# Revit family: MUEBLE SUNSET 600 TEAK
name_source: partatom
category: Generic Models
units: mm (PartAtom-declared; Revit-internal decimal feet)

## family parameters
Always vertical = Yes
Can host rebar = No
Cut with Voids When Loaded = No
Part Type = Normal
Room Calculation Point = No
Round Connector Dimension = Use Diameter
Shared = No
Work Plane-Based = No

## types (12) — shared parameters
Ancho tirador = 250 mm  [stored 0.82021 ft]
Material cubierta = Loza blanco brillo
Material tirador = Acero semi pulido
Profundidad receptáculo = 150 mm

## per-type parameters (varying)
| type | Ancho | Ancho borde cub | Largo | Largo receptáculo | Material costados | Material frentes | Prof borde cub trasero | Prof lavamanos |
| ORANS Mueble Orlando Fume (MFC 034) 060,5cm ancho | 480 mm  [stored 1.5748 ft] | 40 mm | 600 mm | 460 mm  [stored 1.50919 ft] | Fume (MFC 034) vertical | Fume (MFC 034) horizontal | 120 mm  [stored 0.393701 ft] | 320 mm  [stored 1.04987 ft] |
| ORANS Mueble Orlando Fume (MFC 034) 070,5cm ancho | 465 mm | 70 mm | 705 mm | 460 mm  [stored 1.50919 ft] | Fume (MFC 034) vertical | Fume (MFC 034) horizontal | 115 mm | 275 mm |
| ORANS Mueble Orlando Fume (MFC 034) 080,5cm ancho | 465 mm | 70 mm | 805 mm | 460 mm  [stored 1.50919 ft] | Fume (MFC 034) vertical | Fume (MFC 034) horizontal | 115 mm | 275 mm |
| ORANS Mueble Orlando Fume (MFC 034) 100,5cm ancho | 465 mm | 70 mm | 1050 mm | 460 mm  [stored 1.50919 ft] | Fume (MFC 034) vertical | Fume (MFC 034) horizontal | 115 mm | 275 mm |
| ORANS Mueble Orlando Haya Light (MFC 030) 060,5cm ancho | 465 mm | 70 mm | 605 mm | 426 mm | Haya Light (MFC 030) vertical | Haya Light (MFC 030) horizontal | 115 mm | 275 mm |
| ORANS Mueble Orlando Haya Light (MFC 030) 070,5cm ancho | 465 mm | 70 mm | 705 mm | 460 mm  [stored 1.50919 ft] | Haya Light (MFC 030) vertical | Haya Light (MFC 030) horizontal | 115 mm | 275 mm |
| ORANS Mueble Orlando Haya Light (MFC 030) 080,5cm ancho | 465 mm | 70 mm | 805 mm | 460 mm  [stored 1.50919 ft] | Haya Light (MFC 030) vertical | Haya Light (MFC 030) horizontal | 115 mm | 275 mm |
| ORANS Mueble Orlando Haya Light (MFC 030) 100,5cm ancho | 465 mm | 70 mm | 1050 mm | 460 mm  [stored 1.50919 ft] | Haya Light (MFC 030) vertical | Haya Light (MFC 030) horizontal | 115 mm | 275 mm |
| ORANS Mueble Orlando Oak 1 (MFC 005) 060,5cm ancho | 465 mm | 70 mm | 605 mm | 426 mm | Oak1 (MFC 005) vertical | Oak1 (MFC 005) horizontal | 115 mm | 275 mm |
| ORANS Mueble Orlando Oak 1 (MFC 005) 070,5cm ancho | 465 mm | 70 mm | 705 mm | 460 mm  [stored 1.50919 ft] | Oak1 (MFC 005) vertical | Oak1 (MFC 005) horizontal | 115 mm | 275 mm |
| ORANS Mueble Orlando Oak 1 (MFC 005) 080,5cm ancho | 465 mm | 70 mm | 805 mm | 460 mm  [stored 1.50919 ft] | Oak1 (MFC 005) vertical | Oak1 (MFC 005) horizontal | 115 mm | 275 mm |
| ORANS Mueble Orlando Oak 1 (MFC 005) 100,5cm ancho | 465 mm | 70 mm | 1050 mm | 460 mm  [stored 1.50919 ft] | Oak1 (MFC 005) vertical | Oak1 (MFC 005) horizontal | 115 mm | 275 mm |

note: [stored X ft] marks values corroborated as IEEE doubles in the binary element streams (Revit-internal decimal feet)

## geometry (parser evidence)
native form markers: Blend x2, Sweep x6
no freeform markers — native parametric forms only
